# Revit family: 06-84-0035-DN40-600
name_source: partatom
category: Pipe Accessories
units: mm (PartAtom-declared; Revit-internal decimal feet)

## family parameters
Always vertical = No
Cut with Voids When Loaded = No
OmniClass Number = 23.60.00.00
OmniClass Title = General Purpose: Services
Part Type = Valve - Breaks Into
Round Connector Dimension = Use Diameter
Shared = Yes
Work Plane-Based = No

## types (17) — shared parameters
Body_Wallthickness = 15 mm  [stored 0.0492126 ft]
DN040_PN10/16 = 06-040-84-0136499
DN050_PN10/16 = 06-050-84-0136499
DN065_PN10/16 = 06-065-84-0136499
DN080_PN10/16 = 06-080-84-0136499
DN100_PN10/16 = 06-100-84-0136499
DN125_PN10/16 = 06-125-84-0136499
DN150_PN10/16 = 06-150-84-0136499
DN200_PN10 = 06-200-84-0036499
DN200_PN16 = 06-200-84-0136499
DN250_PN10 = 06-250-84-0036499
DN250_PN16 = 06-250-84-0136499
DN300_PN10 = 06-300-84-0036487
DN300_PN16 = 06-300-84-0136487
DN350_PN10 = 06-350-84-003
DN350_PN16 = 06-350-84-013
DN450_PN10 = 06-450-84-003
DN450_PN16 = 06-450-84-013
DN500_PN10 = 06-500-84-003
DN500_PN16 = 06-500-84-013
DN600_PN10 = 06-600-84-003
DN600_PN16 = 06-600-84-013
Ftc = 4 mm  [stored 0.0131234 ft]
Gearbox_Flangethickness = 15 mm  [stored 0.0492126 ft]
Name_Height_reference = 10 mm  [stored 0.0328084 ft]
Rib_Thickness = 18 mm  [stored 0.0590551 ft]
Search_table = 06-84-0035-DN40-600
Tf = 26 mm
zero-valued in all types: Bottom_Reference

## per-type parameters (varying)
- DN 040: At=55.5 mm; Body_Height=100 mm; Body_depth=111 mm; Body_width=58 mm; Bonnet_Flange_Depth=126 mm; Bonnet_Flange_Width=78 mm; Bonnet_Flange_cut=7.5 mm  [stored 0.0246063 ft]; Bonnet_Flange_thickness=15 mm  [stored 0.0492126 ft]; Bonnet_Height=37.5 mm; Bonnet_Reference_height=90 mm; Bonnet_Thickness=59.16 mm; Bt=59.16 mm; Bt_2=52 mm; CL=49 mm; CL _Thickness=5.5 mm; CL_2=19 mm  [stored 0.062336 ft]; CL_Thickness 2=1 mm  [stored 0.00328084 ft]; Cut_Reference=280 mm; DN 040=Yes; DN 050=No; DN 065=No; DN 080=No; DN 100=No; DN 125=No; DN 150=No; DN 200=No; DN 250=No; DN 300=No; DN 350=No; DN 400=No; DN 450=No; DN 500=No; DN 600=No; DN400_PN10=06-400-84-003; DN400_PN16=06-400-84-013; Description_=AVK_GATE_VALVE,FLANGED; F=7 mm  [stored 0.0229659 ft]; F1=8 mm  [stored 0.0262467 ft]; F2=30 mm; Fillet_Thickness=6 mm  [stored 0.019685 ft]; Flange_OR=75 mm; Flange_Thickness=19 mm  [stored 0.062336 ft]; Flange_Thickness_cut=27.5 mm; Ftc_reference_height=75 mm; Gearbox_Flange_Dia=8 mm  [stored 0.0262467 ft]; H=194 mm; H3=269 mm; Horizontal_Flange_width=150 mm; ID (Radius)=20 mm  [stored 0.0656168 ft]; L=140 mm; L_Dia=40 mm; Name_Reference=80 mm; Name_Width=29 mm; Nominal Diameter (DN)=40 mm; R1tv=750 mm; R2f=15 mm  [stored 0.0492126 ft]; RF_Dia=42 mm; Rf=250 mm; Rib_Height_Reference_1=120 mm; Rib_Height_Reference_2=110 mm; Rib_Height_Reference_3=100 mm; Rib_Height_Reference_4=40 mm; Rib_Width_1=29 mm; Rib_Width_2=29 mm; Rib_Width_3=29 mm; Rib_depth_1=29 mm; Rib_depth_2=29 mm; Rib_depth_3=29 mm; Rt=250 mm; URL product pages=https://www.avkvalves.com
- DN 050: At=60.5 mm; Body_Height=110 mm; Body_depth=121 mm; Body_width=58 mm; Bonnet_Flange_Depth=133 mm; Bonnet_Flange_Width=81 mm; Bonnet_Flange_cut=7.5 mm  [stored 0.0246063 ft]; Bonnet_Flange_thickness=15 mm  [stored 0.0492126 ft]; Bonnet_Height=41.25 mm; Bonnet_Reference_height=100 mm; Bonnet_Thickness=59.16 mm; Bt=59.16 mm; Bt_2=52 mm; CL=53 mm; CL _Thickness=6 mm  [stored 0.019685 ft]; CL_2=23 mm; CL_Thickness 2=2 mm  [stored 0.00656168 ft]; Cut_Reference=300 mm; DN 040=No; DN 050=Yes; DN 065=No; DN 080=No; DN 100=No; DN 125=No; DN 150=No; DN 200=No; DN 250=No; DN 300=No; DN 350=No; DN 400=No; DN 450=No; DN 500=No; DN 600=No; DN400_PN10=06-400-84-003; DN400_PN16=06-400-84-013; Description_=AVK_GATE_VALVE,FLANGED; F=7 mm  [stored 0.0229659 ft]; F1=8 mm  [stored 0.0262467 ft]; F2=30 mm; Fillet_Thickness=6 mm  [stored 0.019685 ft]; Flange_OR=82.5 mm; Flange_Thickness=19 mm  [stored 0.062336 ft]; Flange_Thickness_cut=28.75 mm; Ftc_reference_height=82.5 mm; Gearbox_Flange_Dia=8 mm  [stored 0.0262467 ft]; H=208 mm; H3=290 mm; Horizontal_Flange_width=164 mm; ID (Radius)=25 mm; L=150 mm; L_Dia=50 mm; Name_Reference=90 mm; Name_Width=29 mm; Nominal Diameter (DN)=50 mm; R1tv=825 mm; R2f=15 mm  [stored 0.0492126 ft]; RF_Dia=50 mm; Rf=273.33 mm; Rib_Height_Reference_1=120 mm; Rib_Height_Reference_2=110 mm; Rib_Height_Reference_3=100 mm; Rib_Height_Reference_4=60 mm; Rib_Width_1=29 mm; Rib_Width_2=29 mm; Rib_Width_3=29 mm; Rib_depth_1=29 mm; Rib_depth_2=29 mm; Rib_depth_3=29 mm; Rt=275 mm; URL product pages=https://www.avkvalves.com
- DN 065: At=68.5 mm; Body_Height=125 mm; Body_depth=137 mm; Body_width=59 mm; Bonnet_Flange_Depth=152 mm; Bonnet_Flange_Width=78 mm; Bonnet_Flange_cut=7.5 mm  [stored 0.0246063 ft]; Bonnet_Flange_thickness=15 mm  [stored 0.0492126 ft]; Bonnet_Height=46.25 mm; Bonnet_Reference_height=115 mm; Bonnet_Thickness=60.18 mm; Bt=60.18 mm; Bt_2=53 mm; CL=70 mm; CL _Thickness=5.5 mm; CL_2=40 mm; CL_Thickness 2=1 mm  [stored 0.00328084 ft]; Cut_Reference=340 mm; DN 040=No; DN 050=No; DN 065=Yes; DN 080=Yes; DN 100=Yes; DN 125=Yes; DN 150=Yes; DN 200=Yes; DN 250=Yes; DN 300=Yes; DN 350=Yes; DN 400=Yes; DN 450=Yes; DN 500=Yes; DN 600=Yes; DN400_PN10=06-400-84-003; DN400_PN16=06-400-84-013; Description_=AVK_GATE-VALVE,FLANGED; F=8.5 mm  [stored 0.0278871 ft]; F1=10 mm  [stored 0.0328084 ft]; F2=34 mm; Fillet_Thickness=6 mm  [stored 0.019685 ft]; Flange_OR=92.5 mm; Flange_Thickness=19 mm  [stored 0.062336 ft]; Flange_Thickness_cut=30 mm; Ftc_reference_height=92.5 mm; Gearbox_Flange_Dia=10 mm  [stored 0.0328084 ft]; H=244 mm; H3=337 mm; Horizontal_Flange_width=186 mm; ID (Radius)=32.5 mm; L=170 mm; L_Dia=65 mm; Name_Reference=100 mm; Name_Width=29.5 mm; Nominal Diameter (DN)=65 mm; R1tv=925 mm; R2f=15 mm  [stored 0.0492126 ft]; RF_Dia=59 mm; Rf=310 mm; Rib_Height_Reference_1=120 mm; Rib_Height_Reference_2=110 mm; Rib_Height_Reference_3=100 mm; Rib_Height_Reference_4=75 mm; Rib_Width_1=29.5 mm; Rib_Width_2=29.5 mm; Rib_Width_3=29.5 mm; Rib_depth_1=29.5 mm; Rib_depth_2=29.5 mm; Rib_depth_3=29.5 mm; Rt=308.33 mm; URL product pages=https://www.avk.com
- DN 080: At=70 mm; Body_Height=155 mm; Body_depth=140 mm; Body_width=58 mm; Bonnet_Flange_Depth=171 mm; Bonnet_Flange_Width=96 mm; Bonnet_Flange_cut=7.5 mm  [stored 0.0246063 ft]; Bonnet_Flange_thickness=15 mm  [stored 0.0492126 ft]; Bonnet_Height=50 mm; Bonnet_Reference_height=145 mm; Bonnet_Thickness=59.16 mm; Bt=59.16 mm; Bt_2=52 mm; CL=78 mm; CL _Thickness=8.5 mm  [stored 0.0278871 ft]; CL_2=48 mm; CL_Thickness 2=7 mm  [stored 0.0229659 ft]; Cut_Reference=360 mm; DN 040=Yes; DN 050=Yes; DN 065=Yes; DN 080=Yes; DN 100=Yes; DN 125=Yes; DN 150=Yes; DN 200=Yes; DN 250=Yes; DN 300=Yes; DN 350=Yes; DN 400=Yes; DN 450=Yes; DN 500=Yes; DN 600=Yes; DN400_PN10=06-400-84-003; DN400_PN16=06-400-84-013; Description_=AVK_GATE_VALVE,FLANGED; F=8.5 mm  [stored 0.0278871 ft]; F1=10 mm  [stored 0.0328084 ft]; F2=34 mm; Fillet_Thickness=6 mm  [stored 0.019685 ft]; Flange_OR=100 mm; Flange_Thickness=19 mm  [stored 0.062336 ft]; Flange_Thickness_cut=30 mm; Ftc_reference_height=100 mm; Gearbox_Flange_Dia=10 mm  [stored 0.0328084 ft]; H=282 mm; H3=382 mm; Horizontal_Flange_width=200 mm; ID (Radius)=40 mm; L=180 mm; L_Dia=80 mm; Name_Reference=130 mm; Name_Width=29 mm; Nominal Diameter (DN)=80 mm; R1tv=1000 mm; R2f=15 mm  [stored 0.0492126 ft]; RF_Dia=66 mm; Rf=333.33 mm; Rib_Height_Reference_1=120 mm; Rib_Height_Reference_2=110 mm; Rib_Height_Reference_3=100 mm; Rib_Height_Reference_4=85 mm; Rib_Width_1=29 mm; Rib_Width_2=29 mm; Rib_Width_3=29 mm; Rib_depth_1=29 mm; Rib_depth_2=29 mm; Rib_depth_3=29 mm; Rt=333.33 mm; URL product pages=https://www.avkvalves.com
- DN 100: At=84 mm; Body_Height=175 mm; Body_depth=168 mm; Body_width=58 mm; Bonnet_Flange_Depth=192 mm; Bonnet_Flange_Width=85 mm; Bonnet_Flange_cut=7.5 mm  [stored 0.0246063 ft]; Bonnet_Flange_thickness=15 mm  [stored 0.0492126 ft]; Bonnet_Height=55 mm; Bonnet_Reference_height=165 mm; Bonnet_Thickness=59.16 mm; Bt=59.16 mm; Bt_2=52 mm; CL=81 mm; CL _Thickness=6.67 mm; CL_2=51 mm; CL_Thickness 2=3.33 mm; Cut_Reference=380 mm; DN 040=Yes; DN 050=Yes; DN 065=Yes; DN 080=Yes; DN 100=Yes; DN 125=Yes; DN 150=Yes; DN 200=Yes; DN 250=Yes; DN 300=Yes; DN 350=Yes; DN 400=Yes; DN 450=Yes; DN 500=Yes; DN 600=Yes; DN400_PN10=06-400-84-003; DN400_PN16=06-400-84-013; Description_=AVK_GATE_VALVE,FLANGED; F=9.5 mm  [stored 0.031168 ft]; F1=11 mm  [stored 0.0360892 ft]; F2=34 mm; Fillet_Thickness=6 mm  [stored 0.019685 ft]; Flange_OR=110 mm; Flange_Thickness=19 mm  [stored 0.062336 ft]; Flange_Thickness_cut=30 mm; Ftc_reference_height=110 mm; Gearbox_Flange_Dia=11 mm  [stored 0.0360892 ft]; H=305 mm; H3=415 mm; Horizontal_Flange_width=220 mm; ID (Radius)=50 mm; L=190 mm; L_Dia=100 mm; Name_Reference=150 mm; Name_Width=29 mm; Nominal Diameter (DN)=100 mm; R1tv=1100 mm; R2f=15 mm  [stored 0.0492126 ft]; RF_Dia=78 mm; Rf=366.67 mm; Rib_Height_Reference_1=120 mm; Rib_Height_Reference_2=110 mm; Rib_Height_Reference_3=100 mm; Rib_Height_Reference_4=90 mm; Rib_Width_1=29 mm; Rib_Width_2=29 mm; Rib_Width_3=29 mm; Rib_depth_1=29 mm; Rib_depth_2=29 mm; Rib_depth_3=29 mm; Rt=366.67 mm; URL product pages=https://www.avkvalves.com
- DN 150: At=121 mm; Body_Height=200 mm; Body_depth=242 mm; Body_width=70 mm; Bonnet_Flange_Depth=272 mm; Bonnet_Flange_Width=119 mm; Bonnet_Flange_cut=7.5 mm  [stored 0.0246063 ft]; Bonnet_Flange_thickness=15 mm  [stored 0.0492126 ft]; Bonnet_Height=71.25 mm; Bonnet_Reference_height=190 mm; Bonnet_Thickness=71.4 mm; Bt=71.4 mm; Bt_2=64 mm; CL=152 mm; CL _Thickness=12.33 mm; CL_2=122 mm; CL_Thickness 2=14.67 mm; Cut_Reference=420 mm; DN 040=Yes; DN 050=Yes; DN 065=Yes; DN 080=Yes; DN 100=Yes; DN 125=Yes; DN 150=Yes; DN 200=Yes; DN 250=Yes; DN 300=Yes; DN 350=Yes; DN 400=Yes; DN 450=Yes; DN 500=Yes; DN 600=Yes; DN400_PN10=06-400-84-003; DN400_PN16=06-400-84-013; Description_=AVK_GATE_VALVE,FLANGED; F=9.5 mm  [stored 0.031168 ft]; F1=11 mm  [stored 0.0360892 ft]; F2=34 mm; Fillet_Thickness=12 mm  [stored 0.0393701 ft]; Flange_OR=142.5 mm; Flange_Thickness=19 mm  [stored 0.062336 ft]; Flange_Thickness_cut=33.75 mm; Ftc_reference_height=142.5 mm; Gearbox_Flange_Dia=11 mm  [stored 0.0360892 ft]; H=401 mm; H3=543 mm; Horizontal_Flange_width=284 mm; ID (Radius)=75 mm; L=210 mm; L_Dia=150 mm; Name_Reference=170 mm; Name_Width=35 mm; Nominal Diameter (DN)=150 mm; R1tv=1425 mm; R2f=30 mm; RF_Dia=106 mm; Rf=473.33 mm; Rib_Height_Reference_1=120 mm; Rib_Height_Reference_2=110 mm; Rib_Height_Reference_3=100 mm; Rib_Height_Reference_4=150 mm; Rib_Width_1=35 mm; Rib_Width_2=35 mm; Rib_Width_3=35 mm; Rib_depth_1=35 mm; Rib_depth_2=35 mm; Rib_depth_3=35 mm; Rt=475 mm; URL product pages=https://www.avkvalves.com
- DN 200: At=165 mm; Body_Height=250 mm; Body_depth=330 mm; Body_width=110 mm; Bonnet_Flange_Depth=332 mm; Bonnet_Flange_Width=134 mm; Bonnet_Flange_cut=12.5 mm  [stored 0.0410105 ft]; Bonnet_Flange_thickness=25 mm; Bonnet_Height=85 mm; Bonnet_Reference_height=240 mm; Bonnet_Thickness=112.2 mm; Bt=112.2 mm; Bt_2=104 mm; CL=191 mm; CL _Thickness=14.83 mm; CL_2=161 mm; CL_Thickness 2=19.67 mm; Cut_Reference=460 mm; DN 040=Yes; DN 050=Yes; DN 065=Yes; DN 080=Yes; DN 100=Yes; DN 125=Yes; DN 150=Yes; DN 200=Yes; DN 250=Yes; DN 300=Yes; DN 350=Yes; DN 400=Yes; DN 450=Yes; DN 500=Yes; DN 600=Yes; DN400_PN10=06-400-84-003; DN400_PN16=06-400-84-013; Description_=AVK_GATE_VALVE,FLANGED; F=12 mm  [stored 0.0393701 ft]; F1=14 mm  [stored 0.0459318 ft]; F2=34 mm; Fillet_Thickness=24 mm  [stored 0.0787402 ft]; Flange_OR=170 mm; Flange_Thickness=20 mm  [stored 0.0656168 ft]; Flange_Thickness_cut=35 mm; Ftc_reference_height=170 mm; Gearbox_Flange_Dia=14 mm  [stored 0.0459318 ft]; H=490 mm; H3=660 mm; Horizontal_Flange_width=340 mm; ID (Radius)=100 mm; L=230 mm; L_Dia=200 mm; Name_Reference=200 mm; Name_Width=55 mm; Nominal Diameter (DN)=200 mm; R1tv=1700 mm; R2f=60 mm; RF_Dia=133 mm; Rf=566.67 mm; Rib_Height_Reference_1=120 mm; Rib_Height_Reference_2=110 mm; Rib_Height_Reference_3=100 mm; Rib_Height_Reference_4=180 mm; Rib_Width_1=55 mm; Rib_Width_2=55 mm; Rib_Width_3=55 mm; Rib_depth_1=55 mm; Rib_depth_2=55 mm; Rib_depth_3=55 mm; Rt=566.67 mm; URL product pages=https://www.avkvalves.com
- DN 250: At=196 mm; Body_Height=320 mm; Body_depth=392 mm; Body_width=132 mm; Bonnet_Flange_Depth=422 mm; Bonnet_Flange_Width=161 mm; Bonnet_Flange_cut=12.5 mm  [stored 0.0410105 ft]; Bonnet_Flange_thickness=25 mm; Bonnet_Height=100 mm; Bonnet_Reference_height=310 mm; Bonnet_Thickness=134.64 mm; Bt=134.64 mm; Bt_2=126 mm; CL=243 mm; CL _Thickness=19.33 mm; CL_2=213 mm; CL_Thickness 2=28.67 mm; Cut_Reference=500 mm; DN 040=Yes; DN 050=Yes; DN 065=Yes; DN 080=Yes; DN 100=Yes; DN 125=Yes; DN 150=Yes; DN 200=Yes; DN 250=Yes; DN 300=Yes; DN 350=Yes; DN 400=Yes; DN 450=Yes; DN 500=Yes; DN 600=Yes; DN400_PN10=06-400-84-003; DN400_PN16=06-400-84-013; Description_=AVK_GATE_VALVE,FLANGED; F=13.5 mm  [stored 0.0442913 ft]; F1=15.5 mm  [stored 0.050853 ft]; F2=47 mm; Fillet_Thickness=24 mm  [stored 0.0787402 ft]; Flange_OR=200 mm; Flange_Thickness=22 mm  [stored 0.0721785 ft]; Flange_Thickness_cut=37.5 mm; Ftc_reference_height=200 mm; Gearbox_Flange_Dia=15.5 mm  [stored 0.050853 ft]; H=625 mm; H3=820 mm; Horizontal_Flange_width=390 mm; ID (Radius)=125 mm; L=250 mm; L_Dia=250 mm; Name_Reference=200 mm; Name_Width=66 mm; Nominal Diameter (DN)=250 mm; R1tv=2000 mm; R2f=60 mm; RF_Dia=160 mm; Rf=650 mm; Rib_Height_Reference_1=90 mm; Rib_Height_Reference_2=110 mm; Rib_Height_Reference_3=100 mm; Rib_Height_Reference_4=250 mm; Rib_Width_1=150 mm; Rib_Width_2=66 mm; Rib_Width_3=66 mm; Rib_depth_1=422 mm; Rib_depth_2=66 mm; Rib_depth_3=66 mm; Rt=666.67 mm; URL product pages=https://www.avkvalves.com
- DN 300: At=209 mm; Body_Height=415 mm; Body_depth=418 mm; Body_width=160 mm; Bonnet_Flange_Depth=448 mm; Bonnet_Flange_Width=180 mm; Bonnet_Flange_cut=17.5 mm  [stored 0.0574147 ft]; Bonnet_Flange_thickness=35 mm; Bonnet_Height=113.75 mm; Bonnet_Reference_height=405 mm; Bonnet_Thickness=163.2 mm; Bt=163.2 mm; Bt_2=154 mm; CL=229 mm; CL _Thickness=22.5 mm  [stored 0.0738189 ft]; CL_2=199 mm; CL_Thickness 2=35 mm; Cut_Reference=540 mm; DN 040=Yes; DN 050=Yes; DN 065=Yes; DN 080=Yes; DN 100=Yes; DN 125=Yes; DN 150=Yes; DN 200=Yes; DN 250=Yes; DN 300=Yes; DN 350=Yes; DN 400=Yes; DN 450=Yes; DN 500=Yes; DN 600=Yes; DN400_PN10=06-350-84-013; DN400_PN16=06-400-30-016; Description_=AVK_GATE_VALVE,FLANGED; F=13.5 mm  [stored 0.0442913 ft]; F1=15.5 mm  [stored 0.050853 ft]; F2=47 mm; Fillet_Thickness=24 mm  [stored 0.0787402 ft]; Flange_OR=227.5 mm; Flange_Thickness=24.5 mm  [stored 0.0803806 ft]; Flange_Thickness_cut=38.75 mm; Ftc_reference_height=227.5 mm; Gearbox_Flange_Dia=15.5 mm  [stored 0.050853 ft]; H=706 mm; H3=929 mm; Horizontal_Flange_width=446 mm; ID (Radius)=150 mm; L=270 mm; L_Dia=300 mm; Name_Reference=300 mm; Name_Width=80 mm; Nominal Diameter (DN)=300 mm; R1tv=2275 mm; R2f=60 mm; RF_Dia=185 mm; Rf=743.33 mm; Rib_Height_Reference_1=113 mm; Rib_Height_Reference_2=285 mm; Rib_Height_Reference_3=100 mm; Rib_Height_Reference_4=325 mm; Rib_Width_1=210 mm; Rib_Width_2=210 mm; Rib_Width_3=80 mm; Rib_depth_1=431 mm; Rib_depth_2=431 mm; Rib_depth_3=80 mm; Rt=758.33 mm; URL product pages=https://www.avkvalves.com
- DN 350: At=238 mm; Body_Height=550 mm; Body_depth=476 mm; Body_width=172 mm; Bonnet_Flange_Depth=554 mm; Bonnet_Flange_Width=206 mm; Bonnet_Flange_cut=17.5 mm  [stored 0.0574147 ft]; Bonnet_Flange_thickness=35 mm; Bonnet_Height=130 mm; Bonnet_Reference_height=540 mm; Bonnet_Thickness=175.44 mm; Bt=175.44 mm; Bt_2=166 mm; CL=304 mm; CL _Thickness=26.83 mm; CL_2=274 mm; CL_Thickness 2=43.67 mm; Cut_Reference=580 mm; DN 040=Yes; DN 050=Yes; DN 065=Yes; DN 080=Yes; DN 100=Yes; DN 125=Yes; DN 150=Yes; DN 200=Yes; DN 250=Yes; DN 300=Yes; DN 350=Yes; DN 400=Yes; DN 450=Yes; DN 500=Yes; DN 600=Yes; DN400_PN10=06-400-84-003; DN400_PN16=06-400-84-013; Description_=AVK_GATE_VALVE,FLANGED; F=16 mm  [stored 0.0524934 ft]; F1=18.5 mm  [stored 0.0606955 ft]; F2=55 mm; Fillet_Thickness=24 mm  [stored 0.0787402 ft]; Flange_OR=260 mm; Flange_Thickness=26.5 mm; Flange_Thickness_cut=42.5 mm; Ftc_reference_height=260 mm; Gearbox_Flange_Dia=18.5 mm  [stored 0.0606955 ft]; H=924 mm; H3=1184 mm; Horizontal_Flange_width=520 mm; ID (Radius)=175 mm; L=290 mm; L_Dia=350 mm; Name_Reference=520 mm; Name_Width=86 mm; Nominal Diameter (DN)=350 mm; R1tv=2600 mm; R2f=60 mm; RF_Dia=215 mm; Rf=866.67 mm; Rib_Height_Reference_1=84 mm; Rib_Height_Reference_2=204 mm; Rib_Height_Reference_3=338 mm; Rib_Height_Reference_4=459 mm; Rib_Width_1=206 mm; Rib_Width_2=206 mm; Rib_Width_3=206 mm; Rib_depth_1=564 mm; Rib_depth_2=564 mm; Rib_depth_3=564 mm; Rt=866.67 mm; URL product pages=https://www.avkvalves.com
- DN 400: At=275 mm; Body_Height=535 mm; Body_depth=550 mm; Body_width=172 mm; Bonnet_Flange_Depth=544 mm; Bonnet_Flange_Width=200 mm; Bonnet_Flange_cut=35 mm; Bonnet_Flange_thickness=70 mm; Bonnet_Height=145 mm; Bonnet_Reference_height=525 mm; Bonnet_Thickness=175.44 mm; Bt=175.44 mm; Bt_2=166 mm; CL=346 mm; CL _Thickness=25.83 mm; CL_2=316 mm; CL_Thickness 2=41.67 mm; Cut_Reference=620 mm; DN 040=Yes; DN 050=Yes; DN 065=Yes; DN 080=Yes; DN 100=Yes; DN 125=Yes; DN 150=Yes; DN 200=Yes; DN 250=Yes; DN 300=Yes; DN 350=Yes; DN 400=Yes; DN 450=Yes; DN 500=Yes; DN 600=Yes; DN400_PN10=06-400-84-003; DN400_PN16=06-400-84-013; Description_=AVK_GATE_VALVE,FLANGED; F=16 mm  [stored 0.0524934 ft]; F1=18.5 mm  [stored 0.0606955 ft]; F2=55 mm; Fillet_Thickness=32 mm; Flange_OR=290 mm; Flange_Thickness=28 mm; Flange_Thickness_cut=45 mm; Ftc_reference_height=290 mm; Gearbox_Flange_Dia=18.5 mm  [stored 0.0606955 ft]; H=951 mm; H3=1248 mm; Horizontal_Flange_width=594 mm; ID (Radius)=200 mm; L=310 mm; L_Dia=400 mm; Name_Reference=475 mm; Name_Width=86 mm; Nominal Diameter (DN)=400 mm; R1tv=2900 mm; R2f=80 mm; RF_Dia=240 mm; Rf=990 mm; Rib_Height_Reference_1=91 mm; Rib_Height_Reference_2=230 mm; Rib_Height_Reference_3=380 mm; Rib_Height_Reference_4=492 mm; Rib_Width_1=200 mm; Rib_Width_2=200 mm; Rib_Width_3=200 mm; Rib_depth_1=564 mm; Rib_depth_2=564 mm; Rib_depth_3=564 mm; Rt=966.67 mm; URL product pages=https://www.avkvalves.com
- DN 450: At=357.5 mm; Body_Height=702 mm; Body_depth=715 mm; Body_width=160 mm; Bonnet_Flange_Depth=787 mm; Bonnet_Flange_Width=194 mm; Bonnet_Flange_cut=35 mm; Bonnet_Flange_thickness=70 mm; Bonnet_Height=160 mm; Bonnet_Reference_height=692 mm; Bonnet_Thickness=163.2 mm; Bt=163.2 mm; Bt_2=154 mm; CL=370 mm; CL _Thickness=24.83 mm; CL_2=340 mm; CL_Thickness 2=39.67 mm; Cut_Reference=660 mm; DN 040=Yes; DN 050=Yes; DN 065=Yes; DN 080=Yes; DN 100=Yes; DN 125=Yes; DN 150=Yes; DN 200=Yes; DN 250=Yes; DN 300=Yes; DN 350=Yes; DN 400=Yes; DN 450=Yes; DN 500=Yes; DN 600=Yes; DN400_PN10=06-400-84-003; DN400_PN16=06-400-84-013; Description_=AVK_GATE_VALVE,FLANGED; F=15 mm  [stored 0.0492126 ft]; F1=18.5 mm  [stored 0.0606955 ft]; F2=83 mm; Fillet_Thickness=32 mm; Flange_OR=320 mm; Flange_Thickness=30 mm; Flange_Thickness_cut=47.5 mm; Ftc_reference_height=320 mm; Gearbox_Flange_Dia=87.5 mm; H=1170 mm; H3=1487 mm; Horizontal_Flange_width=634 mm; ID (Radius)=225 mm; L=330 mm; L_Dia=450 mm; Name_Reference=665 mm; Name_Width=80 mm; Nominal Diameter (DN)=450 mm; R1tv=3200 mm; R2f=80 mm; RF_Dia=274 mm; Rf=1056.67 mm; Rib_Height_Reference_1=172 mm; Rib_Height_Reference_2=330 mm; Rib_Height_Reference_3=475 mm; Rib_Height_Reference_4=595 mm; Rib_Width_1=186 mm; Rib_Width_2=186 mm; Rib_Width_3=186 mm; Rib_depth_1=814 mm; Rib_depth_2=814 mm; Rib_depth_3=814 mm; Rt=1066.67 mm; URL product pages=https://www.avkvalves.com
- DN 500-PN10: At=359.5 mm; Body_Height=650 mm; Body_depth=719 mm; Body_width=187 mm; Bonnet_Flange_Depth=791 mm; Bonnet_Flange_Width=227 mm; Bonnet_Flange_cut=35 mm; Bonnet_Flange_thickness=70 mm; Bonnet_Height=178.75 mm; Bonnet_Reference_height=640 mm; Bonnet_Thickness=190.74 mm; Bt=190.74 mm; Bt_2=181 mm; CL=397 mm; CL _Thickness=30.33 mm; CL_2=367 mm; CL_Thickness 2=50.67 mm; Cut_Reference=700 mm; DN 040=Yes; DN 050=Yes; DN 065=Yes; DN 080=Yes; DN 100=Yes; DN 125=Yes; DN 150=Yes; DN 200=Yes; DN 250=Yes; DN 300=Yes; DN 350=Yes; DN 400=Yes; DN 450=Yes; DN 500=Yes; DN 600=Yes; DN400_PN10=06-400-84-003; DN400_PN16=06-400-84-013; Description_=AVK_GATE_VALVE,FLANGED; F=15 mm  [stored 0.0492126 ft]; F1=18.5 mm  [stored 0.0606955 ft]; F2=78 mm; Fillet_Thickness=32 mm; Flange_OR=357.5 mm; Flange_Thickness=31.5 mm; Flange_Thickness_cut=53.73 mm; Ftc_reference_height=357.5 mm; Gearbox_Flange_Dia=87.5 mm; H=1140 mm; H3=1500 mm; Horizontal_Flange_width=720 mm; ID (Radius)=250.05 mm; L=350 mm; L_Dia=500.1 mm; Name_Reference=590 mm; Name_Width=93.5 mm; Nominal Diameter (DN)=500.1 mm; R1tv=3575 mm; R2f=80 mm; RF_Dia=291 mm; Rf=1200 mm; Rib_Height_Reference_1=153 mm; Rib_Height_Reference_2=350 mm; Rib_Height_Reference_3=500 mm; Rib_Height_Reference_4=600 mm; Rib_Width_1=221 mm; Rib_Width_2=221 mm; Rib_Width_3=221 mm; Rib_depth_1=834 mm; Rib_depth_2=834 mm; Rib_depth_3=834 mm; Rt=1191.67 mm; URL product pages=https://www.avkvalves.com
- DN 600-PN10: At=420 mm; Body_Height=740 mm; Body_depth=840 mm; Body_width=190 mm; Bonnet_Flange_Depth=891 mm; Bonnet_Flange_Width=182 mm; Bonnet_Flange_cut=35 mm; Bonnet_Flange_thickness=70 mm; Bonnet_Height=210 mm; Bonnet_Reference_height=730 mm; Bonnet_Thickness=193.8 mm; Bt=193.8 mm; Bt_2=184 mm; CL=450 mm; CL _Thickness=22.83 mm; CL_2=420 mm; CL_Thickness 2=35.67 mm; Cut_Reference=780 mm; DN 040=Yes; DN 050=Yes; DN 065=Yes; DN 080=Yes; DN 100=Yes; DN 125=Yes; DN 150=Yes; DN 200=Yes; DN 250=Yes; DN 300=Yes; DN 350=Yes; DN 400=Yes; DN 450=Yes; DN 500=Yes; DN 600=Yes; DN400_PN10=06-400-84-003; DN400_PN16=06-400-84-013; Description_=AVK_GATE_VALVE,FLANGED; F=15 mm  [stored 0.0492126 ft]; F1=18.5 mm  [stored 0.0606955 ft]; F2=85 mm; Fillet_Thickness=32 mm; Flange_OR=420 mm; Flange_Thickness=36 mm; Flange_Thickness_cut=59.98 mm; Ftc_reference_height=420 mm; Gearbox_Flange_Dia=87.5 mm; H=1290 mm; H3=1705 mm; Horizontal_Flange_width=830 mm; ID (Radius)=300.05 mm; L=390 mm; L_Dia=600.1 mm; Name_Reference=655 mm; Name_Width=95 mm; Nominal Diameter (DN)=600.1 mm; R1tv=4200 mm; R2f=80 mm; RF_Dia=360 mm; Rf=1383.33 mm; Rib_Height_Reference_1=180 mm; Rib_Height_Reference_2=308 mm; Rib_Height_Reference_3=491 mm; Rib_Height_Reference_4=674 mm; Rib_Width_1=182 mm; Rib_Width_2=182 mm; Rib_Width_3=182 mm; Rib_depth_1=964 mm; Rib_depth_2=964 mm; Rib_depth_3=964 mm; Rt=1400 mm; URL product pages=https://www.avkvalves.com
- DN 125: At=96 mm; Body_Height=190 mm; Body_depth=192 mm; Body_width=58 mm; Bonnet_Flange_Depth=220 mm; Bonnet_Flange_Width=88 mm; Bonnet_Flange_cut=7.5 mm  [stored 0.0246063 ft]; Bonnet_Flange_thickness=15 mm  [stored 0.0492126 ft]; Bonnet_Height=62.5 mm; Bonnet_Reference_height=180 mm; Bonnet_Thickness=59.16 mm; Bt=59.16 mm; Bt_2=52 mm; CL=107 mm; CL _Thickness=7.17 mm; CL_2=77 mm; CL_Thickness 2=4.33 mm; Cut_Reference=400 mm; DN 040=Yes; DN 050=Yes; DN 065=Yes; DN 080=Yes; DN 100=Yes; DN 125=Yes; DN 150=Yes; DN 200=Yes; DN 250=Yes; DN 300=Yes; DN 350=Yes; DN 400=Yes; DN 450=Yes; DN 500=Yes; DN 600=Yes; DN400_PN10=06-400-84-003; DN400_PN16=06-400-84-013; Description_=AVK_GATE_VALVE,FLANGED; F=9.5 mm  [stored 0.031168 ft]; F1=11 mm  [stored 0.0360892 ft]; F2=34 mm; Fillet_Thickness=6 mm  [stored 0.019685 ft]; Flange_OR=125 mm; Flange_Thickness=19 mm  [stored 0.062336 ft]; Flange_Thickness_cut=31.25 mm; Ftc_reference_height=125 mm; Gearbox_Flange_Dia=11 mm  [stored 0.0360892 ft]; H=346 mm; H3=471 mm; Horizontal_Flange_width=250 mm; ID (Radius)=62.5 mm; L=200 mm; L_Dia=125 mm; Name_Reference=165 mm; Name_Width=29 mm; Nominal Diameter (DN)=125 mm; R1tv=1250 mm; R2f=15 mm  [stored 0.0492126 ft]; RF_Dia=92 mm; Rf=416.67 mm; Rib_Height_Reference_1=120 mm; Rib_Height_Reference_2=110 mm; Rib_Height_Reference_3=100 mm; Rib_Height_Reference_4=120 mm; Rib_Width_1=29 mm; Rib_Width_2=29 mm; Rib_Width_3=29 mm; Rib_depth_1=29 mm; Rib_depth_2=29 mm; Rib_depth_3=29 mm; Rt=416.67 mm; URL product pages=https://www.avkvalves.com
- DN 500-PN16: At=359.5 mm; Body_Height=650 mm; Body_depth=719 mm; Body_width=187 mm; Bonnet_Flange_Depth=792 mm; Bonnet_Flange_Width=227 mm; Bonnet_Flange_cut=35 mm; Bonnet_Flange_thickness=70 mm; Bonnet_Height=178.75 mm; Bonnet_Reference_height=640 mm; Bonnet_Thickness=190.74 mm; Bt=190.74 mm; Bt_2=181 mm; CL=399 mm; CL _Thickness=30.33 mm; CL_2=369 mm; CL_Thickness 2=50.67 mm; Cut_Reference=700 mm; DN 040=Yes; DN 050=Yes; DN 065=Yes; DN 080=Yes; DN 100=Yes; DN 125=Yes; DN 150=Yes; DN 200=Yes; DN 250=Yes; DN 300=Yes; DN 350=Yes; DN 400=Yes; DN 450=Yes; DN 500=Yes; DN 600=Yes; DN400_PN10=06-400-84-003; DN400_PN16=06-400-84-013; Description_=AVK_GATE_VALVE,FLANGED; F=15 mm  [stored 0.0492126 ft]; F1=18.5 mm  [stored 0.0606955 ft]; F2=78 mm; Fillet_Thickness=32 mm; Flange_OR=357.5 mm; Flange_Thickness=31.5 mm; Flange_Thickness_cut=53.71 mm; Ftc_reference_height=357.5 mm; Gearbox_Flange_Dia=87.5 mm; H=1142 mm; H3=1500 mm; Horizontal_Flange_width=716 mm; ID (Radius)=250.08 mm; L=350 mm; L_Dia=500.16 mm; Name_Reference=590 mm; Name_Width=93.5 mm; Nominal Diameter (DN)=500.16 mm; R1tv=3575 mm; R2f=80 mm; RF_Dia=291 mm; Rf=1193.33 mm; Rib_Height_Reference_1=153 mm; Rib_Height_Reference_2=350 mm; Rib_Height_Reference_3=500 mm; Rib_Height_Reference_4=600 mm; Rib_Width_1=221 mm; Rib_Width_2=221 mm; Rib_Width_3=221 mm; Rib_depth_1=834 mm; Rib_depth_2=834 mm; Rib_depth_3=834 mm; Rt=1191.67 mm; URL product pages=https://www.avkvalves.com
- DN 600-PN16: At=420 mm; Body_Height=740 mm; Body_depth=840 mm; Body_width=190 mm; Bonnet_Flange_Depth=891 mm; Bonnet_Flange_Width=182 mm; Bonnet_Flange_cut=35 mm; Bonnet_Flange_thickness=70 mm; Bonnet_Height=210 mm; Bonnet_Reference_height=730 mm; Bonnet_Thickness=193.8 mm; Bt=193.8 mm; Bt_2=184 mm; CL=445 mm; CL _Thickness=22.83 mm; CL_2=415 mm; CL_Thickness 2=35.67 mm; Cut_Reference=780 mm; DN 040=Yes; DN 050=Yes; DN 065=Yes; DN 080=Yes; DN 100=Yes; DN 125=Yes; DN 150=Yes; DN 200=Yes; DN 250=Yes; DN 300=Yes; DN 350=Yes; DN 400=Yes; DN 450=Yes; DN 500=Yes; DN 600=Yes; DN400_PN10=06-400-84-003; DN400_PN16=06-400-84-013; Description_=AVK_GATE_VALVE,FLANGED; F=15 mm  [stored 0.0492126 ft]; F1=18.5 mm  [stored 0.0606955 ft]; F2=85 mm; Fillet_Thickness=32 mm; Flange_OR=420 mm; Flange_Thickness=36 mm; Flange_Thickness_cut=59.96 mm; Ftc_reference_height=420 mm; Gearbox_Flange_Dia=87.5 mm; H=1285 mm; H3=1705 mm; Horizontal_Flange_width=840 mm; ID (Radius)=300.08 mm; L=390 mm; L_Dia=600.16 mm; Name_Reference=655 mm; Name_Width=95 mm; Nominal Diameter (DN)=600.16 mm; R1tv=4200 mm; R2f=80 mm; RF_Dia=360 mm; Rf=1400 mm; Rib_Height_Reference_1=180 mm; Rib_Height_Reference_2=308 mm; Rib_Height_Reference_3=491 mm; Rib_Height_Reference_4=674 mm; Rib_Width_1=182 mm; Rib_Width_2=182 mm; Rib_Width_3=182 mm; Rib_depth_1=964 mm; Rib_depth_2=964 mm; Rib_depth_3=964 mm; Rt=1400 mm; URL product pages=https://www.avkvalves.com

note: [stored X ft] marks values corroborated as IEEE doubles in the binary element streams (Revit-internal decimal feet)

## geometry (parser evidence)
native form markers: Sweep x4
no freeform markers — native parametric forms only
